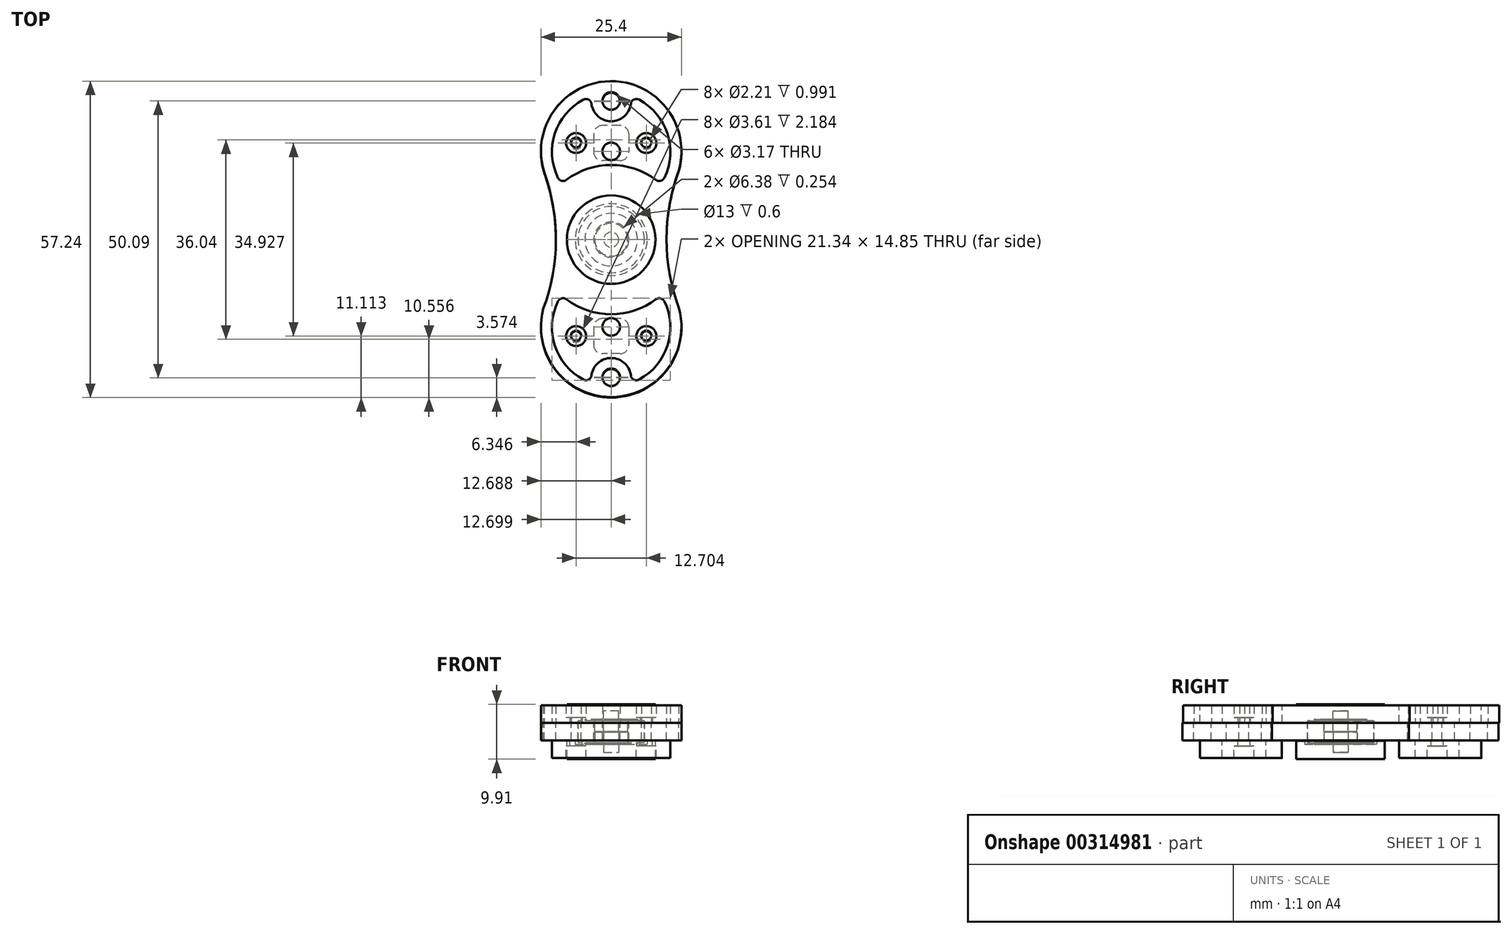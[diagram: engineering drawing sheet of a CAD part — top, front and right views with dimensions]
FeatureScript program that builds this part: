
annotation { "Feature Type Name" : "Feature", "Feature Type Description" : "" }
export const myFeature = defineFeature(function(context is Context, id is Id, definition is map)
    precondition{}
    {
        {
            var Q0;
            Q0=qCreatedBy(makeId("Top.planeOp"),FACE);
            cPlane(context, id + "F0", {"entities" : qUnion([Q0]), "cplaneType" : CPlaneType.OFFSET, "offset" : 3.17 * mm, "oppositeDirection" : true, "width" : 150 * mm, "height" : 150 * mm});
        }
        {
            var Q0;
            Q0=qCreatedBy(makeId("Top.planeOp"),FACE);
            cPlane(context, id + "F1", {"entities" : qUnion([Q0]), "cplaneType" : CPlaneType.OFFSET, "offset" : 1.59 * mm, "oppositeDirection" : true, "width" : 150 * mm, "height" : 150 * mm});
        }
        {
            var Q0;
            Q0=qCreatedBy(makeId("Top.planeOp"),FACE);
            var sketch = newSketch(context, id + "F2", { "sketchPlane" : qUnion([Q0])});
            skArc(sketch, "E0", {"start": v(11.75, 11.05) * mm, "mid": v(0.14, 28.57) * mm, "end": v(-11.85, 11.3) * mm});
            skArc(sketch, "E1", {"start": v(-11.68, -10.88) * mm, "mid": v(-0.1, -28.57) * mm, "end": v(11.75, -11.05) * mm});
            skArc(sketch, "E2", {"start": v(12.21, 12.4) * mm, "mid": v(10, 0) * mm, "end": v(12.21, -12.4) * mm});
            skPoint(sketch, "E2.first.point", {"position": v(10, 0) * mm});
            skPoint(sketch, "E2.second.point", {"position": v(81.6, 0) * mm});
            skPoint(sketch, "E2.third.point", {"position": v(43.2, -35.71) * mm});
            skArc(sketch, "E3", {"start": v(-12.27, -12.6) * mm, "mid": v(-10, -0.26) * mm, "end": v(-12.13, 12.1) * mm});
            skPoint(sketch, "E3.first.point", {"position": v(-10, 0) * mm});
            skPoint(sketch, "E3.second.point", {"position": v(-81.6, 0) * mm});
            skPoint(sketch, "E3.third.point", {"position": v(-50.18, -35.59) * mm});
            skCircle(sketch, "E4", {"center": v(6.35, 17.46) * mm, "radius": 0.89 * mm});
            skCircle(sketch, "E5", {"center": v(-6.35, 17.46) * mm, "radius": 0.89 * mm});
            skCircle(sketch, "E6", {"center": v(-6.35, -17.46) * mm, "radius": 0.89 * mm});
            skCircle(sketch, "E7", {"center": v(6.35, -17.46) * mm, "radius": 0.89 * mm});
            skCircle(sketch, "E8", {"center": v(0, 25) * mm, "radius": 1.59 * mm});
            skCircle(sketch, "E9", {"center": v(0, -25) * mm, "radius": 1.59 * mm});
            skLineSegment(sketch, "E10.bottom", {"start": v(1.59, 20.64) * mm, "end": v(-1.59, 20.64) * mm});
            skLineSegment(sketch, "E10.top", {"start": v(1.59, 14.29) * mm, "end": v(-1.59, 14.29) * mm});
            skLineSegment(sketch, "E10.left", {"start": v(3.18, 19.05) * mm, "end": v(3.18, 15.87) * mm});
            skLineSegment(sketch, "E10.right", {"start": v(-3.17, 19.05) * mm, "end": v(-3.17, 15.87) * mm});
            skPoint(sketch, "E10.middle", {"position": v(0, 17.46) * mm});
            skLineSegment(sketch, "E11.bottom", {"start": v(1.59, -14.29) * mm, "end": v(-1.59, -14.29) * mm});
            skLineSegment(sketch, "E11.top", {"start": v(1.59, -20.64) * mm, "end": v(-1.59, -20.64) * mm});
            skLineSegment(sketch, "E11.left", {"start": v(3.18, -15.87) * mm, "end": v(3.18, -19.05) * mm});
            skLineSegment(sketch, "E11.right", {"start": v(-3.17, -15.87) * mm, "end": v(-3.17, -19.05) * mm});
            skPoint(sketch, "E11.middle", {"position": v(0, -17.46) * mm});
            skCircle(sketch, "E12", {"center": v(0, 0) * mm, "radius": 6 * mm});
            skPoint(sketch, "E13.visualSharp", {"position": v(-3.17, 20.64) * mm});
            skArc(sketch, "E13.filletArc", {"start": v(-1.59, 20.64) * mm, "mid": v(-2.71, 20.17) * mm, "end": v(-3.17, 19.05) * mm});
            skPoint(sketch, "E14.visualSharp", {"position": v(3.18, 20.64) * mm});
            skArc(sketch, "E14.filletArc", {"start": v(3.18, 19.05) * mm, "mid": v(2.71, 20.17) * mm, "end": v(1.59, 20.64) * mm});
            skPoint(sketch, "E15.visualSharp", {"position": v(3.18, 14.29) * mm});
            skArc(sketch, "E15.filletArc", {"start": v(1.59, 14.29) * mm, "mid": v(2.71, 14.75) * mm, "end": v(3.18, 15.87) * mm});
            skPoint(sketch, "E16.visualSharp", {"position": v(-3.17, 14.29) * mm});
            skArc(sketch, "E16.filletArc", {"start": v(-3.17, 15.87) * mm, "mid": v(-2.71, 14.75) * mm, "end": v(-1.59, 14.29) * mm});
            skPoint(sketch, "E17.visualSharp", {"position": v(-3.17, -14.29) * mm});
            skArc(sketch, "E17.filletArc", {"start": v(-1.59, -14.29) * mm, "mid": v(-2.71, -14.75) * mm, "end": v(-3.17, -15.87) * mm});
            skPoint(sketch, "E18.visualSharp", {"position": v(3.18, -14.29) * mm});
            skArc(sketch, "E18.filletArc", {"start": v(3.18, -15.87) * mm, "mid": v(2.71, -14.75) * mm, "end": v(1.59, -14.29) * mm});
            skPoint(sketch, "E19.visualSharp", {"position": v(3.18, -20.64) * mm});
            skArc(sketch, "E19.filletArc", {"start": v(1.59, -20.64) * mm, "mid": v(2.71, -20.17) * mm, "end": v(3.17, -19.05) * mm});
            skPoint(sketch, "E20.visualSharp", {"position": v(-3.17, -20.64) * mm});
            skArc(sketch, "E20.filletArc", {"start": v(-3.17, -19.05) * mm, "mid": v(-2.71, -20.17) * mm, "end": v(-1.59, -20.64) * mm});
            skSolve(sketch);
        }
        {
            var Q0;
            Q0=makeQuery(id+"F2.imprint","IMPRINT",FACE,{"disambiguationData":[TD([[makeQuery(id+"F2.imprint","IMPRINT",EDGE,{"derivedFrom":sQuery(id+"F2.wireOp",EDGE,"E4")}),-1.0]])]});
            extrude(context, id + "F3", {"entities" : qUnion([Q0]), "oppositeDirection" : true, "depth" : 3.17 * mm});
        }
        {
            var Q0;
            Q0=qCreatedBy(makeId("Top.planeOp"),FACE);
            var sketch = newSketch(context, id + "F4", { "sketchPlane" : qUnion([Q0])});
            skArc(sketch, "E21", {"start": v(-3.44, 26.02) * mm, "mid": v(0, 21.42) * mm, "end": v(3.42, 26.02) * mm});
            skArc(sketch, "E22", {"start": v(3.42, -26) * mm, "mid": v(0, -21.4) * mm, "end": v(-3.44, -26) * mm});
            skArc(sketch, "E23", {"start": v(-3.44, 26.02) * mm, "mid": v(-10.11, 19.4) * mm, "end": v(-9, 10.08) * mm});
            skArc(sketch, "E24", {"start": v(-9, -10.06) * mm, "mid": v(-10.11, -19.4) * mm, "end": v(-3.44, -26) * mm});
            skLineSegment(sketch, "E25", {"start": v(-10, 0) * mm, "end": v(-10, -0.1) * mm, "construction": true});
            skPoint(sketch, "E26.first.point", {"position": v(10, 0) * mm});
            skPoint(sketch, "E27.first.point", {"position": v(-10, 0) * mm});
            skArc(sketch, "E28", {"start": v(8.98, 10.08) * mm, "mid": v(0, 13.5) * mm, "end": v(-9, 10.08) * mm});
            skCircle(sketch, "E29", {"center": v(-6.35, 17.47) * mm, "radius": 1.8 * mm});
            skCircle(sketch, "E30", {"center": v(6.35, -17.46) * mm, "radius": 1.8 * mm});
            skArc(sketch, "E31.trimOffspring", {"start": v(-9, -10.06) * mm, "mid": v(0, -13.5) * mm, "end": v(8.98, -10.06) * mm});
            skArc(sketch, "E32.trimOffspring", {"start": v(8.98, 10.08) * mm, "mid": v(10.1, 19.4) * mm, "end": v(3.42, 26.02) * mm});
            skArc(sketch, "E33.trimOffspring", {"start": v(3.42, -26) * mm, "mid": v(10.1, -19.4) * mm, "end": v(8.98, -10.06) * mm});
            skArc(sketch, "E34.trimOffspring", {"start": v(-10, -0.1) * mm, "mid": v(-10, -0.05) * mm, "end": v(-10, 0) * mm});
            skCircle(sketch, "E35", {"center": v(6.35, 17.47) * mm, "radius": 1.8 * mm});
            skCircle(sketch, "E36", {"center": v(-6.35, -17.46) * mm, "radius": 1.8 * mm});
            skCircle(sketch, "E37", {"center": v(-6.35, 17.47) * mm, "radius": 1.1 * mm});
            skCircle(sketch, "E38", {"center": v(6.35, 17.47) * mm, "radius": 1.1 * mm});
            skCircle(sketch, "E39", {"center": v(-6.35, -17.46) * mm, "radius": 1.1 * mm});
            skCircle(sketch, "E40", {"center": v(6.35, -17.46) * mm, "radius": 1.1 * mm});
            skSolve(sketch);
        }
        {
            var Q0;
            Q0=makeQuery(id+"F4.imprint","IMPRINT",FACE,{"disambiguationData":[TD([[makeQuery(id+"F4.imprint","IMPRINT",EDGE,{"derivedFrom":sQuery(id+"F4.wireOp",EDGE,"E21")}),-1.0]])]});
            var Q1;
            Q1=makeQuery(id+"F4.imprint","IMPRINT",FACE,{"disambiguationData":[TD([[makeQuery(id+"F4.imprint","IMPRINT",EDGE,{"derivedFrom":sQuery(id+"F4.wireOp",EDGE,"E22")}),-1.0]])]});
            extrude(context, id + "F5", {"entities" : qUnion([Q0, Q1]), "depth" : 3.17 * mm});
        }
        {
            var Q0;
            Q0=makeQuery(id+"F4.imprint","IMPRINT",FACE,{"disambiguationData":[TD([[makeQuery(id+"F4.imprint","IMPRINT",EDGE,{"derivedFrom":sQuery(id+"F4.wireOp",EDGE,"E29")}),1.0]])]});
            var Q1;
            Q1=makeQuery(id+"F4.imprint","IMPRINT",FACE,{"disambiguationData":[TD([[makeQuery(id+"F4.imprint","IMPRINT",EDGE,{"derivedFrom":sQuery(id+"F4.wireOp",EDGE,"E35")}),1.0]])]});
            var Q2;
            Q2=makeQuery(id+"F4.imprint","IMPRINT",FACE,{"disambiguationData":[TD([[makeQuery(id+"F4.imprint","IMPRINT",EDGE,{"derivedFrom":sQuery(id+"F4.wireOp",EDGE,"E36")}),1.0]])]});
            var Q3;
            Q3=makeQuery(id+"F4.imprint","IMPRINT",FACE,{"disambiguationData":[TD([[makeQuery(id+"F4.imprint","IMPRINT",EDGE,{"derivedFrom":sQuery(id+"F4.wireOp",EDGE,"E30")}),1.0]])]});
            extrude(context, id + "F6", {"entities" : qUnion([Q0, Q1, Q2, Q3]), "operationType" : NewBodyOperationType.ADD, "depth" : .9906 * mm});
        }
        {
            var Q0;
            Q0=qCreatedBy(id+"F0.planeOp",FACE);
            var sketch = newSketch(context, id + "F7", { "sketchPlane" : qUnion([Q0])});
            skArc(sketch, "E41", {"start": v(-3.44, 26.02) * mm, "mid": v(-0.01, 21.42) * mm, "end": v(3.42, 26.02) * mm});
            skArc(sketch, "E42", {"start": v(3.42, -26) * mm, "mid": v(-0.01, -21.41) * mm, "end": v(-3.44, -26) * mm});
            skArc(sketch, "E43", {"start": v(-3.44, 26.02) * mm, "mid": v(-10.12, 19.4) * mm, "end": v(-9, 10.08) * mm});
            skArc(sketch, "E44", {"start": v(-9, -10.07) * mm, "mid": v(-10.12, -19.4) * mm, "end": v(-3.44, -26) * mm});
            skLineSegment(sketch, "E45", {"start": v(-10.01, 0) * mm, "end": v(-10.01, -0.1) * mm, "construction": true});
            skArc(sketch, "E46", {"start": v(8.98, 10.08) * mm, "mid": v(-0.01, 13.5) * mm, "end": v(-9, 10.08) * mm});
            skCircle(sketch, "E47", {"center": v(6.35, 17.47) * mm, "radius": 1.8 * mm});
            skCircle(sketch, "E48", {"center": v(-6.35, 17.47) * mm, "radius": 1.8 * mm});
            skArc(sketch, "E49.trimOffspring", {"start": v(-9, -10.07) * mm, "mid": v(-0.01, -13.5) * mm, "end": v(8.98, -10.07) * mm});
            skArc(sketch, "E50.trimOffspring", {"start": v(8.98, 10.08) * mm, "mid": v(10.1, 19.4) * mm, "end": v(3.42, 26.02) * mm});
            skArc(sketch, "E51.trimOffspring", {"start": v(3.42, -26) * mm, "mid": v(10.1, -19.4) * mm, "end": v(8.98, -10.07) * mm});
            skArc(sketch, "E52.trimOffspring", {"start": v(-10.01, -0.1) * mm, "mid": v(-10.01, -0.05) * mm, "end": v(-10.01, 0) * mm});
            skCircle(sketch, "E53", {"center": v(-6.35, -17.46) * mm, "radius": 1.8 * mm});
            skCircle(sketch, "E54", {"center": v(6.35, -17.46) * mm, "radius": 1.8 * mm});
            skCircle(sketch, "E55", {"center": v(-6.35, -17.46) * mm, "radius": 1.1 * mm});
            skCircle(sketch, "E56", {"center": v(6.35, -17.46) * mm, "radius": 1.1 * mm});
            skCircle(sketch, "E57", {"center": v(-6.35, 17.47) * mm, "radius": 1.1 * mm});
            skCircle(sketch, "E58", {"center": v(6.35, 17.47) * mm, "radius": 1.1 * mm});
            skSolve(sketch);
        }
        {
            var Q0;
            Q0=makeQuery(id+"F7.imprint","IMPRINT",FACE,{"disambiguationData":[TD([[makeQuery(id+"F7.imprint","IMPRINT",EDGE,{"derivedFrom":sQuery(id+"F7.wireOp",EDGE,"E42")}),-1.0]])]});
            var Q1;
            Q1=makeQuery(id+"F7.imprint","IMPRINT",FACE,{"disambiguationData":[TD([[makeQuery(id+"F7.imprint","IMPRINT",EDGE,{"derivedFrom":sQuery(id+"F7.wireOp",EDGE,"E41")}),-1.0]])]});
            extrude(context, id + "F8", {"entities" : qUnion([Q0, Q1]), "oppositeDirection" : true, "depth" : 3.17 * mm});
        }
        {
            var Q0;
            Q0=makeQuery(id+"F7.imprint","IMPRINT",FACE,{"disambiguationData":[TD([[makeQuery(id+"F7.imprint","IMPRINT",EDGE,{"derivedFrom":sQuery(id+"F7.wireOp",EDGE,"E48")}),1.0]])]});
            var Q1;
            Q1=makeQuery(id+"F7.imprint","IMPRINT",FACE,{"disambiguationData":[TD([[makeQuery(id+"F7.imprint","IMPRINT",EDGE,{"derivedFrom":sQuery(id+"F7.wireOp",EDGE,"E47")}),1.0]])]});
            var Q2;
            Q2=makeQuery(id+"F7.imprint","IMPRINT",FACE,{"disambiguationData":[TD([[makeQuery(id+"F7.imprint","IMPRINT",EDGE,{"derivedFrom":sQuery(id+"F7.wireOp",EDGE,"E53")}),1.0]])]});
            var Q3;
            Q3=makeQuery(id+"F7.imprint","IMPRINT",FACE,{"disambiguationData":[TD([[makeQuery(id+"F7.imprint","IMPRINT",EDGE,{"derivedFrom":sQuery(id+"F7.wireOp",EDGE,"E54")}),1.0]])]});
            extrude(context, id + "F9", {"entities" : qUnion([Q0, Q1, Q2, Q3]), "operationType" : NewBodyOperationType.ADD, "oppositeDirection" : true, "depth" : .9906 * mm});
        }
        {
            var Q0;
            Q0=makeQuery(id+"F5.opExtrude","SWEPT_EDGE",EDGE,{"disambiguationData":[OSD([sQuery(id+"F4.wireOp",EDGE,"E21"),sQuery(id+"F4.wireOp",EDGE,"E32.trimOffspring")])]});
            var Q1;
            Q1=makeQuery(id+"F5.opExtrude","SWEPT_EDGE",EDGE,{"disambiguationData":[OSD([sQuery(id+"F4.wireOp",EDGE,"E21"),sQuery(id+"F4.wireOp",EDGE,"E23")])]});
            var Q2;
            Q2=makeQuery(id+"F5.opExtrude","SWEPT_EDGE",EDGE,{"disambiguationData":[OSD([sQuery(id+"F4.wireOp",EDGE,"E24"),sQuery(id+"F4.wireOp",EDGE,"E31.trimOffspring")])]});
            var Q3;
            Q3=makeQuery(id+"F5.opExtrude","SWEPT_EDGE",EDGE,{"disambiguationData":[OSD([sQuery(id+"F4.wireOp",EDGE,"E31.trimOffspring"),sQuery(id+"F4.wireOp",EDGE,"E33.trimOffspring")])]});
            var Q4;
            Q4=makeQuery(id+"F5.opExtrude","SWEPT_EDGE",EDGE,{"disambiguationData":[OSD([sQuery(id+"F4.wireOp",EDGE,"E28"),sQuery(id+"F4.wireOp",EDGE,"E32.trimOffspring")])]});
            var Q5;
            Q5=makeQuery(id+"F5.opExtrude","SWEPT_EDGE",EDGE,{"disambiguationData":[OSD([sQuery(id+"F4.wireOp",EDGE,"E23"),sQuery(id+"F4.wireOp",EDGE,"E28")])]});
            var Q6;
            Q6=makeQuery(id+"F5.opExtrude","SWEPT_EDGE",EDGE,{"disambiguationData":[OSD([sQuery(id+"F4.wireOp",EDGE,"E22"),sQuery(id+"F4.wireOp",EDGE,"E33.trimOffspring")])]});
            var Q7;
            Q7=makeQuery(id+"F5.opExtrude","SWEPT_EDGE",EDGE,{"disambiguationData":[OSD([sQuery(id+"F4.wireOp",EDGE,"E22"),sQuery(id+"F4.wireOp",EDGE,"E24")])]});
            var Q8;
            Q8=makeQuery(id+"F8.opExtrude","SWEPT_EDGE",EDGE,{"disambiguationData":[OSD([sQuery(id+"F7.wireOp",EDGE,"E42"),sQuery(id+"F7.wireOp",EDGE,"E51.trimOffspring")])]});
            var Q9;
            Q9=makeQuery(id+"F8.opExtrude","SWEPT_EDGE",EDGE,{"disambiguationData":[OSD([sQuery(id+"F7.wireOp",EDGE,"E42"),sQuery(id+"F7.wireOp",EDGE,"E44")])]});
            var Q10;
            Q10=makeQuery(id+"F8.opExtrude","SWEPT_EDGE",EDGE,{"disambiguationData":[OSD([sQuery(id+"F7.wireOp",EDGE,"E46"),sQuery(id+"F7.wireOp",EDGE,"E50.trimOffspring")])]});
            var Q11;
            Q11=makeQuery(id+"F8.opExtrude","SWEPT_EDGE",EDGE,{"disambiguationData":[OSD([sQuery(id+"F7.wireOp",EDGE,"E43"),sQuery(id+"F7.wireOp",EDGE,"E46")])]});
            var Q12;
            Q12=makeQuery(id+"F8.opExtrude","SWEPT_EDGE",EDGE,{"disambiguationData":[OSD([sQuery(id+"F7.wireOp",EDGE,"E49.trimOffspring"),sQuery(id+"F7.wireOp",EDGE,"E51.trimOffspring")])]});
            var Q13;
            Q13=makeQuery(id+"F8.opExtrude","SWEPT_EDGE",EDGE,{"disambiguationData":[OSD([sQuery(id+"F7.wireOp",EDGE,"E44"),sQuery(id+"F7.wireOp",EDGE,"E49.trimOffspring")])]});
            var Q14;
            Q14=makeQuery(id+"F8.opExtrude","SWEPT_EDGE",EDGE,{"disambiguationData":[OSD([sQuery(id+"F7.wireOp",EDGE,"E41"),sQuery(id+"F7.wireOp",EDGE,"E50.trimOffspring")])]});
            var Q15;
            Q15=makeQuery(id+"F8.opExtrude","SWEPT_EDGE",EDGE,{"disambiguationData":[OSD([sQuery(id+"F7.wireOp",EDGE,"E41"),sQuery(id+"F7.wireOp",EDGE,"E43")])]});
            fillet(context, id + "F10", {"entities" : qUnion([Q0, Q1, Q2, Q3, Q4, Q5, Q6, Q7, Q8, Q9, Q10, Q11, Q12, Q13, Q14, Q15]), "radius" : 1 * mm, "tangentPropagation" : true, "allowEdgeOverflow" : false});
        }
        {
            var Q0;
            Q0=qCreatedBy(id+"F1.planeOp",FACE);
            var sketch = newSketch(context, id + "F11", { "sketchPlane" : qUnion([Q0])});
            skCircle(sketch, "E59", {"center": v(0, 0) * mm, "radius": 6 * mm});
            skCircle(sketch, "E60", {"center": v(0, 0) * mm, "radius": 3 * mm});
            skSolve(sketch);
        }
        {
            var Q0;
            Q0=makeQuery(id+"F11.imprint","IMPRINT",FACE,{"disambiguationData":[TD([[makeQuery(id+"F11.imprint","IMPRINT",EDGE,{"derivedFrom":sQuery(id+"F11.wireOp",EDGE,"E59")}),1.0]])]});
            extrude(context, id + "F12", {"entities" : qUnion([Q0]), "endBound" : BoundingType.SYMMETRIC, "depth" : 4 * mm});
        }
        {
            var Q0;
            Q0=makeQuery(id+"F12.opExtrude","CAP_FACE",FACE,{"disambiguationData":[OSD([sQuery(id+"F11.wireOp",EDGE,"E59"),sQuery(id+"F11.wireOp",EDGE,"E60")])],"isStart":false});
            var sketch = newSketch(context, id + "F13", { "sketchPlane" : qUnion([Q0])});
            skCircle(sketch, "E61", {"center": v(0, 0) * mm, "radius": 3.19 * mm});
            skCircle(sketch, "E62", {"center": v(0, 0) * mm, "radius": 4.76 * mm});
            skSolve(sketch);
        }
        {
            var Q0;
            Q0=makeQuery(id+"F13.imprint","IMPRINT",FACE,{"disambiguationData":[TD([[makeQuery(id+"F13.imprint","IMPRINT",EDGE,{"derivedFrom":sQuery(id+"F13.wireOp",EDGE,"E61")}),-1.0]])]});
            extrude(context, id + "F14", {"entities" : qUnion([Q0]), "depth" : .254 * mm});
        }
        {
            var Q0;
            Q0=qCreatedBy(makeId("Top.planeOp"),FACE);
            var sketch = newSketch(context, id + "F15", { "sketchPlane" : qUnion([Q0])});
            skArc(sketch, "E63", {"start": v(11.75, 11.15) * mm, "mid": v(0.14, 28.67) * mm, "end": v(-11.85, 11.4) * mm});
            skArc(sketch, "E64", {"start": v(-11.68, -10.78) * mm, "mid": v(-0.1, -28.48) * mm, "end": v(11.75, -10.95) * mm});
            skLineSegment(sketch, "E65", {"start": v(16.9, 15.97) * mm, "end": v(-16.39, 15.97) * mm, "construction": true});
            skLineSegment(sketch, "E66", {"start": v(17.82, -15.78) * mm, "end": v(-17.21, -15.78) * mm, "construction": true});
            skLineSegment(sketch, "E67", {"start": v(10, 5.3) * mm, "end": v(10, -4.8) * mm, "construction": true});
            skLineSegment(sketch, "E68", {"start": v(-10, 4.38) * mm, "end": v(-10, -3.6) * mm, "construction": true});
            skArc(sketch, "E69", {"start": v(12.21, 12.5) * mm, "mid": v(10, 0.1) * mm, "end": v(12.21, -12.3) * mm});
            skPoint(sketch, "E69.first.point", {"position": v(10, 0.1) * mm});
            skPoint(sketch, "E69.second.point", {"position": v(81.6, 0.1) * mm});
            skPoint(sketch, "E69.third.point", {"position": v(43.2, -35.61) * mm});
            skArc(sketch, "E70", {"start": v(-12.27, -12.5) * mm, "mid": v(-10, -0.16) * mm, "end": v(-12.13, 12.2) * mm});
            skPoint(sketch, "E70.first.point", {"position": v(-10, 0.1) * mm});
            skPoint(sketch, "E70.second.point", {"position": v(-81.6, 0.1) * mm});
            skPoint(sketch, "E70.third.point", {"position": v(-50.18, -35.5) * mm});
            skCircle(sketch, "E71", {"center": v(6.35, 17.56) * mm, "radius": 0.89 * mm});
            skCircle(sketch, "E72", {"center": v(-6.35, 17.56) * mm, "radius": 0.89 * mm});
            skCircle(sketch, "E73", {"center": v(-6.35, -17.36) * mm, "radius": 0.89 * mm});
            skCircle(sketch, "E74", {"center": v(6.35, -17.36) * mm, "radius": 0.89 * mm});
            skCircle(sketch, "E75", {"center": v(0, 25.1) * mm, "radius": 1.59 * mm});
            skCircle(sketch, "E76", {"center": v(0, -24.9) * mm, "radius": 1.59 * mm});
            skLineSegment(sketch, "E77", {"start": v(12.7, 15.97) * mm, "end": v(12.7, 26.12) * mm, "construction": true});
            skLineSegment(sketch, "E78", {"start": v(12.7, 26.12) * mm, "end": v(12.7, 15.97) * mm, "construction": true});
            skLineSegment(sketch, "E79", {"start": v(12.7, -25.65) * mm, "end": v(12.7, 15.97) * mm, "construction": true});
            skLineSegment(sketch, "E80", {"start": v(-12.7, 15.97) * mm, "end": v(-12.7, 26.12) * mm, "construction": true});
            skLineSegment(sketch, "E81", {"start": v(-12.7, 26.12) * mm, "end": v(-12.7, 15.97) * mm, "construction": true});
            skLineSegment(sketch, "E82", {"start": v(-12.7, 15.97) * mm, "end": v(-12.7, -25.65) * mm, "construction": true});
            skLineSegment(sketch, "E83", {"start": v(-18.48, 17.56) * mm, "end": v(19.2, 17.56) * mm, "construction": true});
            skLineSegment(sketch, "E84", {"start": v(-19.2, -17.36) * mm, "end": v(20.85, -17.36) * mm, "construction": true});
            skPoint(sketch, "E85.middle", {"position": v(0, 17.56) * mm});
            skPoint(sketch, "E86.middle", {"position": v(0, -17.36) * mm});
            skCircle(sketch, "E87", {"center": v(0, 15.97) * mm, "radius": 1.59 * mm});
            skPoint(sketch, "E88.orphan", {"position": v(-3.18, 20.74) * mm});
            skPoint(sketch, "E89.orphan", {"position": v(-3.18, 14.39) * mm});
            skPoint(sketch, "E90.orphan", {"position": v(3.17, 14.39) * mm});
            skPoint(sketch, "E85.left.start.orphan", {"position": v(3.17, 20.74) * mm});
            skCircle(sketch, "E91", {"center": v(0, -15.78) * mm, "radius": 1.59 * mm});
            skPoint(sketch, "E92.orphan", {"position": v(3.17, -14.19) * mm});
            skPoint(sketch, "E86.top.start.orphan", {"position": v(3.17, -20.54) * mm});
            skPoint(sketch, "E93.orphan", {"position": v(-3.18, -20.54) * mm});
            skPoint(sketch, "E86.right.start.orphan", {"position": v(-3.18, -14.19) * mm});
            skCircle(sketch, "E94", {"center": v(0, 0) * mm, "radius": 1.59 * mm});
            skCircle(sketch, "E95", {"center": v(45.8, 0.1) * mm, "radius": 35.8 * mm});
            skCircle(sketch, "E96", {"center": v(-45.8, 0.05) * mm, "radius": 35.8 * mm});
            skSolve(sketch);
        }
        {
            var Q0;
            Q0=makeQuery(id+"F15.imprint","IMPRINT",FACE,{"disambiguationData":[TD([[makeQuery(id+"F15.imprint","IMPRINT",EDGE,{"derivedFrom":sQuery(id+"F15.wireOp",EDGE,"E71")}),-1.0]])]});
            extrude(context, id + "F16", {"entities" : qUnion([Q0]), "depth" : 3.17 * mm});
        }
        {
            var Q0;
            Q0=makeQuery(id+"F14.opExtrude","CAP_FACE",FACE,{"disambiguationData":[OSD([sQuery(id+"F13.wireOp",EDGE,"E61"),sQuery(id+"F13.wireOp",EDGE,"E62")])],"isStart":false});
            var sketch = newSketch(context, id + "F17", { "sketchPlane" : qUnion([Q0])});
            skCircle(sketch, "E97", {"center": v(0, 0) * mm, "radius": 2.98 * mm});
            skCircle(sketch, "E98", {"center": v(0, 0) * mm, "radius": 8 * mm});
            skCircle(sketch, "E99", {"center": v(0, 0) * mm, "radius": 6.5 * mm});
            skCircle(sketch, "E100", {"center": v(0, 0) * mm, "radius": 1.35 * mm});
            skSolve(sketch);
        }
        {
            var Q0;
            Q0=makeQuery(id+"F17.imprint","IMPRINT",FACE,{"disambiguationData":[TD([[makeQuery(id+"F17.imprint","IMPRINT",EDGE,{"derivedFrom":sQuery(id+"F17.wireOp",EDGE,"E97")}),-1.0]])]});
            var Q1;
            Q1=makeQuery(id+"F17.imprint","IMPRINT",FACE,{"disambiguationData":[TD([[makeQuery(id+"F17.imprint","IMPRINT",EDGE,{"derivedFrom":sQuery(id+"F17.wireOp",EDGE,"E97")}),1.0]])]});
            var Q2;
            Q2=makeQuery(id+"F17.imprint","IMPRINT",FACE,{"disambiguationData":[TD([[makeQuery(id+"F17.imprint","IMPRINT",EDGE,{"derivedFrom":makeQuery(id+"F14.opExtrude","CAP_EDGE",EDGE,{"disambiguationData":[OSD([sQuery(id+"F13.wireOp",EDGE,"E61")])],"isStart":false})}),-1.0]])]});
            var Q3;
            Q3=makeQuery(id+"F17.imprint","IMPRINT",FACE,{"disambiguationData":[TD([[makeQuery(id+"F17.imprint","IMPRINT",EDGE,{"derivedFrom":sQuery(id+"F17.wireOp",EDGE,"E99")}),1.0]])]});
            var Q4;
            Q4=makeQuery(id+"F17.imprint","IMPRINT",FACE,{"disambiguationData":[TD([[makeQuery(id+"F17.imprint","IMPRINT",EDGE,{"derivedFrom":sQuery(id+"F17.wireOp",EDGE,"E98")}),1.0]])]});
            var Q5;
            Q5=makeQuery(id+"F17.imprint","IMPRINT",FACE,{"disambiguationData":[TD([[makeQuery(id+"F17.imprint","IMPRINT",EDGE,{"derivedFrom":sQuery(id+"F17.wireOp",EDGE,"E99")}),-1.0]])]});
            var Q6;
            Q6=makeQuery(id+"F17.imprint","IMPRINT",FACE,{"disambiguationData":[TD([[makeQuery(id+"F17.imprint","IMPRINT",EDGE,{"derivedFrom":sQuery(id+"F17.wireOp",EDGE,"E100")}),1.0]])]});
            extrude(context, id + "F18", {"entities" : qUnion([Q0, Q1, Q2, Q3, Q4, Q5, Q6]), "depth" : 2.7 * mm});
        }
        {
            var Q0;
            Q0=makeQuery(id+"F17.imprint","IMPRINT",FACE,{"disambiguationData":[TD([[makeQuery(id+"F17.imprint","IMPRINT",EDGE,{"derivedFrom":sQuery(id+"F17.wireOp",EDGE,"E97")}),1.0]])]});
            extrude(context, id + "F19", {"entities" : qUnion([Q0]), "operationType" : NewBodyOperationType.ADD, "oppositeDirection" : true, "depth" : 2.2 * mm});
        }
        {
            var Q0;
            Q0=makeQuery(id+"F17.imprint","IMPRINT",FACE,{"disambiguationData":[TD([[makeQuery(id+"F17.imprint","IMPRINT",EDGE,{"derivedFrom":sQuery(id+"F17.wireOp",EDGE,"E98")}),1.0]])]});
            extrude(context, id + "F20", {"entities" : qUnion([Q0]), "operationType" : NewBodyOperationType.ADD, "oppositeDirection" : true, "depth" : .6 * mm});
        }
        {
            var Q0;
            Q0=makeQuery(id+"F17.imprint","IMPRINT",FACE,{"disambiguationData":[TD([[makeQuery(id+"F17.imprint","IMPRINT",EDGE,{"derivedFrom":sQuery(id+"F17.wireOp",EDGE,"E100")}),1.0]])]});
            extrude(context, id + "F21", {"entities" : qUnion([Q0]), "operationType" : NewBodyOperationType.REMOVE, "depth" : 1.5 * mm});
        }
        {
            var Q0;
            Q0=makeQuery(id+"F12.opExtrude","CAP_FACE",FACE,{"disambiguationData":[OSD([sQuery(id+"F11.wireOp",EDGE,"E59"),sQuery(id+"F11.wireOp",EDGE,"E60")])],"isStart":true});
            var sketch = newSketch(context, id + "F22", { "sketchPlane" : qUnion([Q0])});
            skCircle(sketch, "E101", {"center": v(0, 0) * mm, "radius": 3.19 * mm});
            skCircle(sketch, "E102", {"center": v(0, 0) * mm, "radius": 4.76 * mm});
            skSolve(sketch);
        }
        {
            var Q0;
            Q0=makeQuery(id+"F22.imprint","IMPRINT",FACE,{"disambiguationData":[TD([[makeQuery(id+"F22.imprint","IMPRINT",EDGE,{"derivedFrom":sQuery(id+"F22.wireOp",EDGE,"E101")}),-1.0]])]});
            extrude(context, id + "F23", {"entities" : qUnion([Q0]), "depth" : .254 * mm});
        }
        {
            var Q0;
            Q0=makeQuery(id+"F23.opExtrude","CAP_FACE",FACE,{"disambiguationData":[OSD([sQuery(id+"F22.wireOp",EDGE,"E101"),sQuery(id+"F22.wireOp",EDGE,"E102")])],"isStart":false});
            var sketch = newSketch(context, id + "F24", { "sketchPlane" : qUnion([Q0])});
            skCircle(sketch, "E103", {"center": v(0, 0) * mm, "radius": 2.98 * mm});
            skCircle(sketch, "E104", {"center": v(0, 0) * mm, "radius": 6.5 * mm});
            skCircle(sketch, "E105", {"center": v(0, 0) * mm, "radius": 8 * mm});
            skCircle(sketch, "E106", {"center": v(0, 0) * mm, "radius": 1.35 * mm});
            skSolve(sketch);
        }
        {
            var Q0;
            Q0=makeQuery(id+"F24.imprint","IMPRINT",FACE,{"disambiguationData":[TD([[makeQuery(id+"F24.imprint","IMPRINT",EDGE,{"derivedFrom":sQuery(id+"F24.wireOp",EDGE,"E103")}),1.0]])]});
            var Q1;
            Q1=makeQuery(id+"F24.imprint","IMPRINT",FACE,{"disambiguationData":[TD([[makeQuery(id+"F24.imprint","IMPRINT",EDGE,{"derivedFrom":sQuery(id+"F24.wireOp",EDGE,"E103")}),-1.0]])]});
            var Q2;
            Q2=makeQuery(id+"F24.imprint","IMPRINT",FACE,{"disambiguationData":[TD([[makeQuery(id+"F24.imprint","IMPRINT",EDGE,{"derivedFrom":makeQuery(id+"F23.opExtrude","CAP_EDGE",EDGE,{"disambiguationData":[OSD([sQuery(id+"F22.wireOp",EDGE,"E101")])],"isStart":false})}),-1.0]])]});
            var Q3;
            Q3=makeQuery(id+"F24.imprint","IMPRINT",FACE,{"disambiguationData":[TD([[makeQuery(id+"F24.imprint","IMPRINT",EDGE,{"derivedFrom":sQuery(id+"F24.wireOp",EDGE,"E104")}),1.0]])]});
            var Q4;
            Q4=makeQuery(id+"F24.imprint","IMPRINT",FACE,{"disambiguationData":[TD([[makeQuery(id+"F24.imprint","IMPRINT",EDGE,{"derivedFrom":sQuery(id+"F24.wireOp",EDGE,"E104")}),-1.0]])]});
            var Q5;
            Q5=makeQuery(id+"F24.imprint","IMPRINT",FACE,{"disambiguationData":[TD([[makeQuery(id+"F24.imprint","IMPRINT",EDGE,{"derivedFrom":sQuery(id+"F24.wireOp",EDGE,"E106")}),1.0]])]});
            extrude(context, id + "F25", {"entities" : qUnion([Q0, Q1, Q2, Q3, Q4, Q5]), "depth" : 2.7 * mm});
        }
        {
            var Q0;
            Q0=makeQuery(id+"F24.imprint","IMPRINT",FACE,{"disambiguationData":[TD([[makeQuery(id+"F24.imprint","IMPRINT",EDGE,{"derivedFrom":sQuery(id+"F24.wireOp",EDGE,"E103")}),1.0]])]});
            extrude(context, id + "F26", {"entities" : qUnion([Q0]), "operationType" : NewBodyOperationType.ADD, "oppositeDirection" : true, "depth" : 2.2 * mm});
        }
        {
            var Q0;
            Q0=makeQuery(id+"F24.imprint","IMPRINT",FACE,{"disambiguationData":[TD([[makeQuery(id+"F24.imprint","IMPRINT",EDGE,{"derivedFrom":sQuery(id+"F24.wireOp",EDGE,"E104")}),-1.0]])]});
            extrude(context, id + "F27", {"entities" : qUnion([Q0]), "operationType" : NewBodyOperationType.ADD, "oppositeDirection" : true, "depth" : .6 * mm});
        }
        {
            var Q0;
            Q0=makeQuery(id+"F24.imprint","IMPRINT",FACE,{"disambiguationData":[TD([[makeQuery(id+"F24.imprint","IMPRINT",EDGE,{"derivedFrom":sQuery(id+"F24.wireOp",EDGE,"E106")}),1.0]])]});
            extrude(context, id + "F28", {"entities" : qUnion([Q0]), "operationType" : NewBodyOperationType.REMOVE, "depth" : 1.5 * mm});
        }
    });
